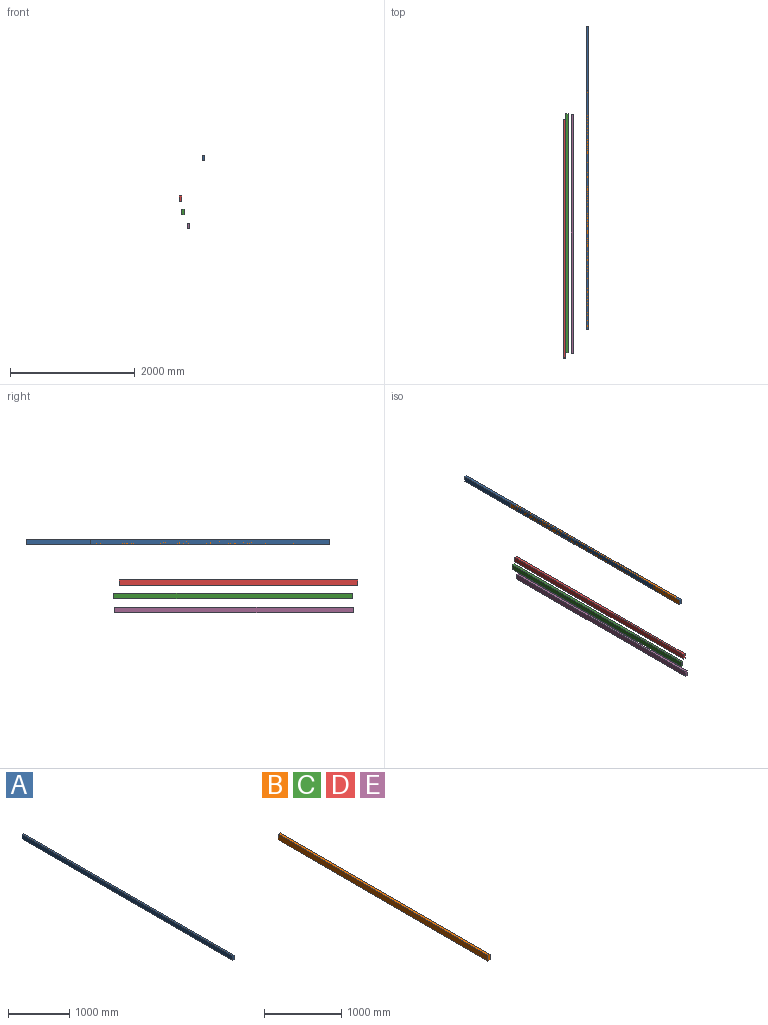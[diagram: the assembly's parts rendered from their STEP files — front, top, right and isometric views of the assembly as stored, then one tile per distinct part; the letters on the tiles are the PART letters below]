
ASSEMBLY  parts=5 mates=1
PART A: 6 faces, bbox 38.1x4876.8x88.9 mm
  f0: plane 4876.8x88.9mm, normal (-1,0,0), area 433547.5mm2, adj f1,f3,f4,f5
  f1: plane 4876.8x38.1mm, normal (0,0,-1), area 185806.1mm2, adj f0,f2,f4,f5
  f2: plane 4876.8x88.9mm, normal (1,0,0), area 433547.5mm2, adj f1,f3,f4,f5
  f3: plane 4876.8x38.1mm, normal (0,0,1), area 185806.1mm2, adj f0,f2,f4,f5
  f4: plane 88.9x38.1mm, normal (0,-1,0), area 3387.1mm2, adj f0,f1,f2,f3
  f5: plane 88.9x38.1mm, normal (0,1,0), area 3387.1mm2, adj f0,f1,f2,f3
PART B: 6 faces, bbox 38.1x3835.4x88.9 mm
  f0: plane 3835.4x88.9mm, normal (-1,0,0), area 340967.1mm2, adj f1,f3,f4,f5
  f1: plane 3835.4x38.1mm, normal (0,0,-1), area 146128.7mm2, adj f0,f2,f4,f5
  f2: plane 3835.4x88.9mm, normal (1,0,0), area 340967.1mm2, adj f1,f3,f4,f5
  f3: plane 3835.4x38.1mm, normal (0,0,1), area 146128.7mm2, adj f0,f2,f4,f5
  f4: plane 88.9x38.1mm, normal (0,-1,0), area 3387.1mm2, adj f0,f1,f2,f3
  f5: plane 88.9x38.1mm, normal (0,1,0), area 3387.1mm2, adj f0,f1,f2,f3
PART C: same geometry as B
PART D: same geometry as B
PART E: same geometry as B
PLACE A t=(-38.1,4876.8,-88.9)mm
PLACE B t=(-38.1,3835.4,-88.9)mm
PLACE C t=(-367.03,3467.44,-958.26)mm
PLACE D t=(-405.21,3381.2,-744.28)mm
PLACE E t=(-282.33,3455.62,-1183.89)mm
MATE fastened B.f2 <-> A.f2  axis (1,0,0) through (0,0,0)mm
